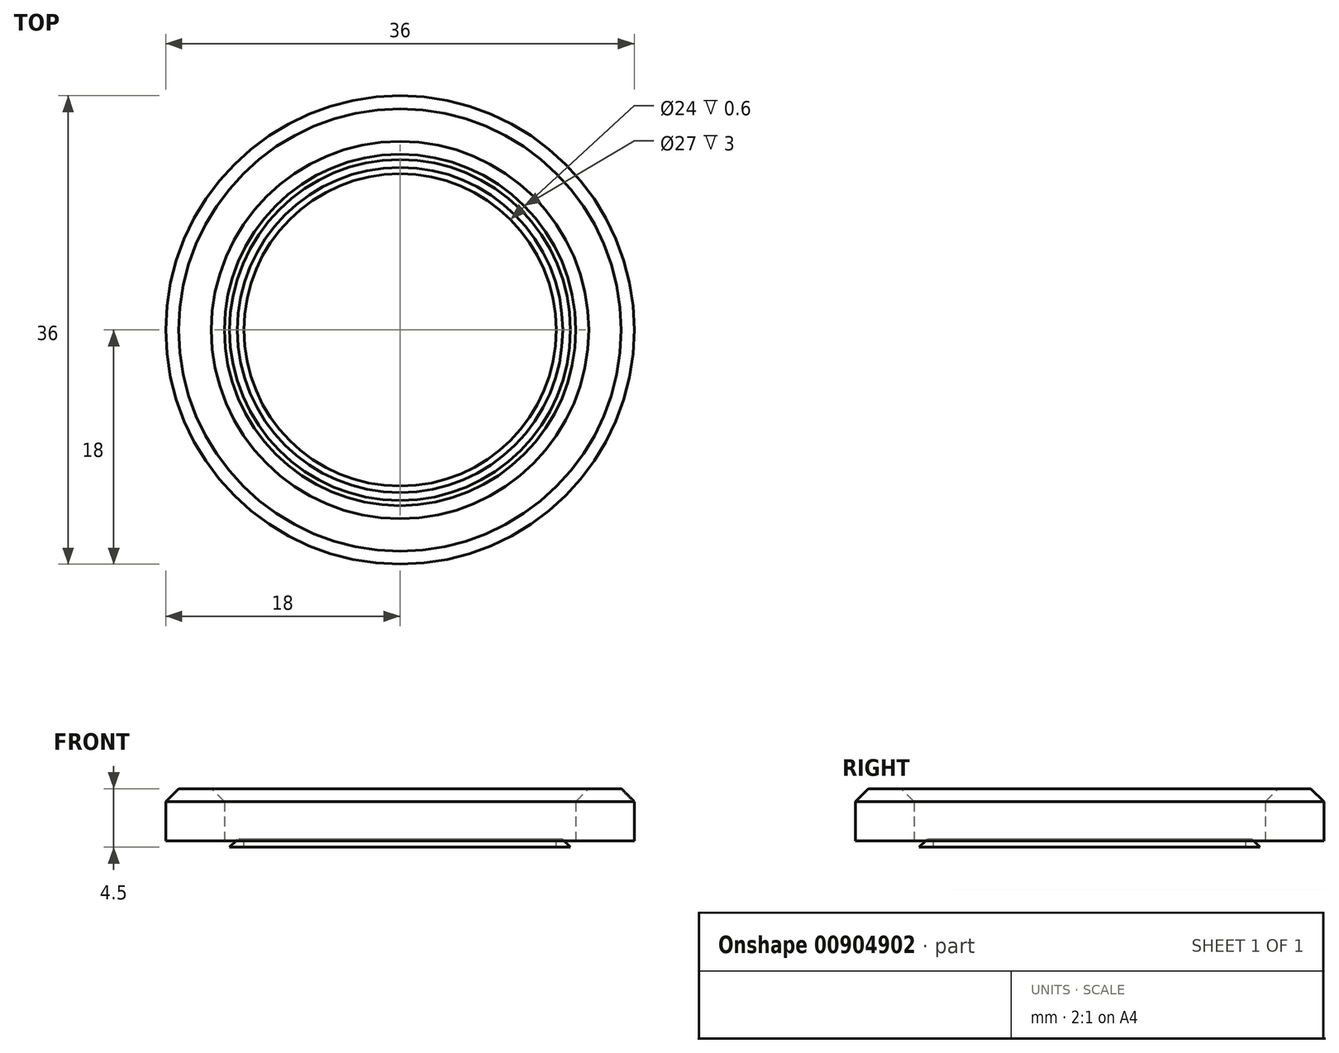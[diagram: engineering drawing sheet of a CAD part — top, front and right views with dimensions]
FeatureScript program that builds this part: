
annotation { "Feature Type Name" : "Feature", "Feature Type Description" : "" }
export const myFeature = defineFeature(function(context is Context, id is Id, definition is map)
    precondition{}
    {
        {
            var Q0;
            Q0=qCreatedBy(makeId("Top.planeOp"),FACE);
            var sketch = newSketch(context, id + "F0", { "sketchPlane" : qUnion([Q0])});
            skCircle(sketch, "E0", {"center": v(0, 0) * mm, "radius": 18 * mm});
            skCircle(sketch, "E1", {"center": v(0, 0) * mm, "radius": 13.5 * mm});
            skCircle(sketch, "E2", {"center": v(0, 0) * mm, "radius": 12 * mm});
            skSolve(sketch);
        }
        {
            var Q0;
            Q0=makeQuery(id+"F0.imprint","IMPRINT",FACE,{"disambiguationData":[TD([[makeQuery(id+"F0.imprint","IMPRINT",EDGE,{"derivedFrom":sQuery(id+"F0.wireOp",EDGE,"E0")}),1.0]])]});
            extrude(context, id + "F1", {"entities" : qUnion([Q0]), "depth" : 4 * mm, "offsetDistance" : 25 * mm});
        }
        {
            var Q0;
            Q0=makeQuery(id+"F0.imprint","IMPRINT",FACE,{"disambiguationData":[TD([[makeQuery(id+"F0.imprint","IMPRINT",EDGE,{"derivedFrom":sQuery(id+"F0.wireOp",EDGE,"E1")}),1.0]])]});
            extrude(context, id + "F2", {"entities" : qUnion([Q0]), "oppositeDirection" : true, "depth" : .5 * mm, "offsetDistance" : 25 * mm, "hasSecondDirection" : true, "secondDirectionOppositeDirection" : false, "secondDirectionDepth" : .1 * mm});
        }
        {
            var Q0;
            Q0=makeQuery(id+"F2.opExtrude","CAP_EDGE",EDGE,{"disambiguationData":[OSD([sQuery(id+"F0.wireOp",EDGE,"E1")])],"isStart":true});
            chamfer(context, id + "F3", {"entities" : qUnion([Q0]), "width" : 1 * mm, "tangentPropagation" : true});
        }
        {
            var Q0;
            Q0=makeQuery(id+"F1.opExtrude","CAP_EDGE",EDGE,{"disambiguationData":[OSD([sQuery(id+"F0.wireOp",EDGE,"E0")])],"isStart":false});
            var Q1;
            Q1=makeQuery(id+"F1.opExtrude","CAP_EDGE",EDGE,{"disambiguationData":[OSD([sQuery(id+"F0.wireOp",EDGE,"E1")])],"isStart":false});
            chamfer(context, id + "F4", {"entities" : qUnion([Q0, Q1]), "width" : 1 * mm, "tangentPropagation" : true});
        }
    });
